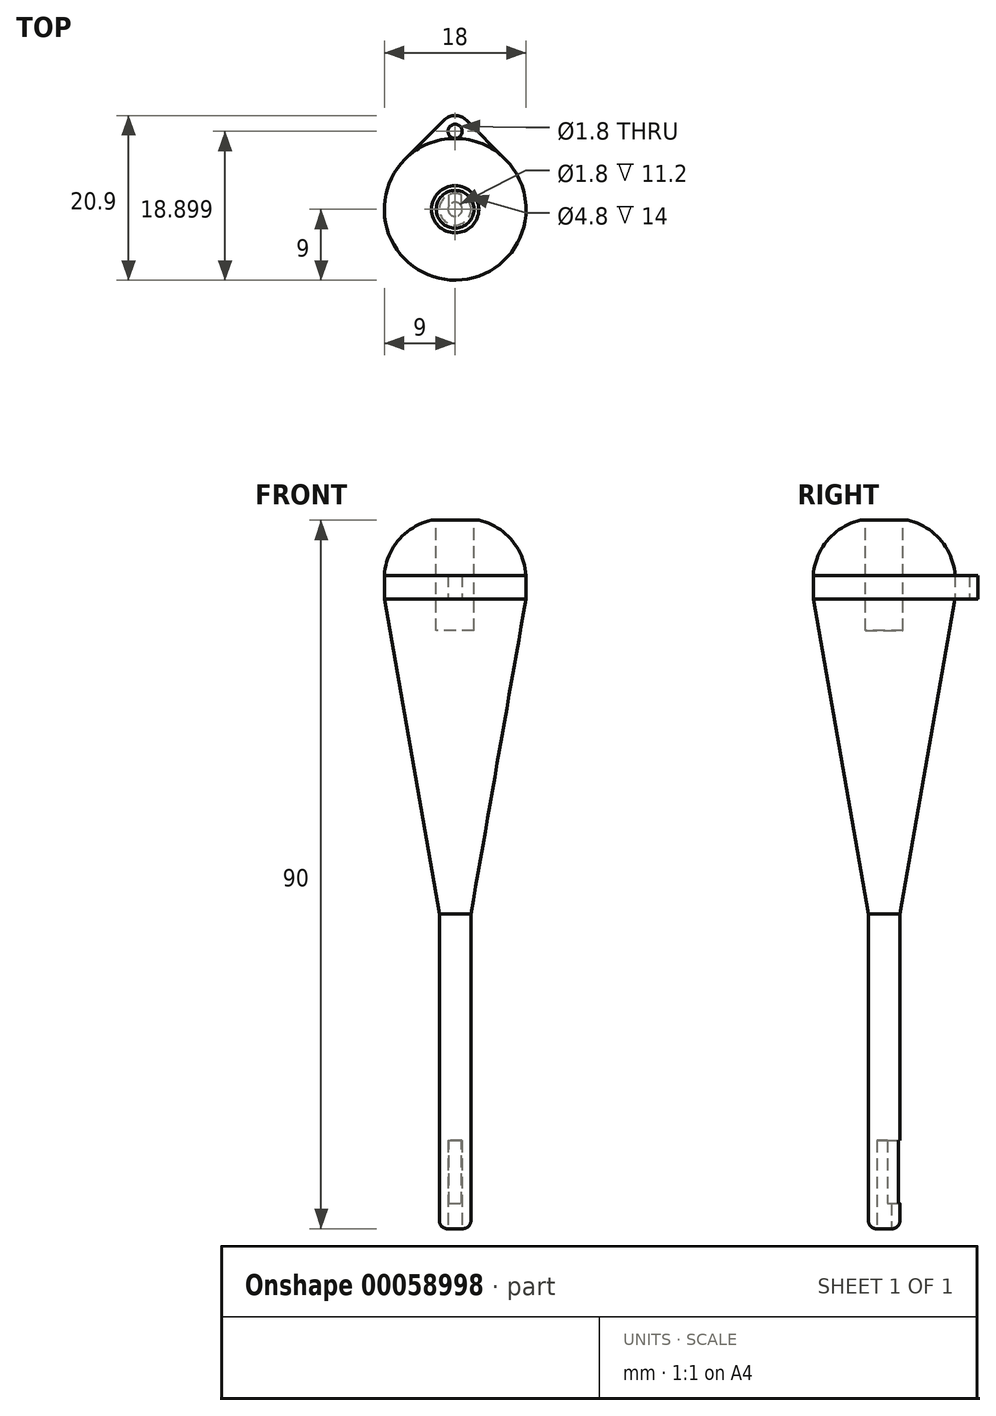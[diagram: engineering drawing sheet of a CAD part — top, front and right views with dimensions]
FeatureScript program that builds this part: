
annotation { "Feature Type Name" : "Feature", "Feature Type Description" : "" }
export const myFeature = defineFeature(function(context is Context, id is Id, definition is map)
    precondition{}
    {
        {
            var Q0;
            Q0=qCreatedBy(makeId("Top.planeOp"),FACE);
            var sketch = newSketch(context, id + "F0", { "sketchPlane" : qUnion([Q0])});
            skArc(sketch, "E0", {"start": v(-6.36, 6.36) * mm, "mid": v(0, -9) * mm, "end": v(6.36, 6.36) * mm});
            skLineSegment(sketch, "E1", {"start": v(-6.36, 6.36) * mm, "end": v(-1.41, 11.31) * mm});
            skLineSegment(sketch, "E2", {"start": v(1.41, 11.31) * mm, "end": v(6.36, 6.36) * mm});
            skPoint(sketch, "E3.visualSharp", {"position": v(0, 12.73) * mm});
            skArc(sketch, "E3.filletArc", {"start": v(1.41, 11.31) * mm, "mid": v(0, 11.9) * mm, "end": v(-1.41, 11.31) * mm});
            skLineSegment(sketch, "E4", {"start": v(0, 0) * mm, "end": v(10.96, 10.96) * mm, "construction": true});
            skCircle(sketch, "E5", {"center": v(0, 0) * mm, "radius": 9 * mm, "construction": true});
            skCircle(sketch, "E6", {"center": v(0, 9.9) * mm, "radius": 0.9 * mm});
            skSolve(sketch);
        }
        {
            var Q0;
            Q0 = qSketchRegion(id + "F0", true);
            extrude(context, id + "F1", {"entities" : qUnion([Q0]), "depth" : 3 * mm});
        }
        {
            var Q0;
            Q0=qCreatedBy(makeId("Right.planeOp"),FACE);
            var sketch = newSketch(context, id + "F2", { "sketchPlane" : qUnion([Q0])});
            skLineSegment(sketch, "E7", {"start": v(0, 3) * mm, "end": v(0, 10) * mm});
            skLineSegment(sketch, "E8", {"start": v(0, 10) * mm, "end": v(3, 10) * mm});
            skLineSegment(sketch, "E9", {"start": v(0, 3) * mm, "end": v(9, 3) * mm});
            skArc(sketch, "E10", {"start": v(9, 3) * mm, "mid": v(7.16, 7.5) * mm, "end": v(3, 10) * mm});
            skLineSegment(sketch, "E11", {"start": v(0, 0) * mm, "end": v(0, -80) * mm});
            skLineSegment(sketch, "E12", {"start": v(0, -80) * mm, "end": v(1, -80) * mm});
            skLineSegment(sketch, "E13", {"start": v(2, -79) * mm, "end": v(2, -40) * mm});
            skLineSegment(sketch, "E14", {"start": v(2, -40) * mm, "end": v(9, 0) * mm});
            skLineSegment(sketch, "E15", {"start": v(9, 0) * mm, "end": v(0, 0) * mm});
            skPoint(sketch, "E16.visualSharp", {"position": v(2, -80) * mm});
            skArc(sketch, "E16.filletArc", {"start": v(1, -80) * mm, "mid": v(1.7, -79.7) * mm, "end": v(2, -79) * mm});
            skSolve(sketch);
        }
        {
            var Q0;
            Q0 = qSketchRegion(id + "F2", true);
            var Q1;
            Q1=sQuery(id+"F2.wireOp",EDGE,"E11");
            revolve(context, id + "F3", {"operationType" : NewBodyOperationType.ADD, "entities" : qUnion([Q0]), "axis" : qUnion([Q1]), "revolveType" : RevolveType.FULL});
        }
        {
            var Q0;
            Q0=qCreatedBy(makeId("Front.planeOp"),FACE);
            cPlane(context, id + "F4", {"entities" : qUnion([Q0]), "cplaneType" : CPlaneType.OFFSET, "offset" : 9 * mm, "oppositeDirection" : true, "width" : 150 * mm, "height" : 150 * mm});
        }
        {
            var Q0;
            Q0=qCreatedBy(id+"F4.planeOp",FACE);
            var sketch = newSketch(context, id + "F5", { "sketchPlane" : qUnion([Q0])});
            skLineSegment(sketch, "E17", {"start": v(0, 0) * mm, "end": v(0, -61.52) * mm, "construction": true});
            skLineSegment(sketch, "E18.bottom", {"start": v(0.8, -76.8) * mm, "end": v(-0.8, -76.8) * mm});
            skLineSegment(sketch, "E18.top", {"start": v(0.8, -68.8) * mm, "end": v(-0.8, -68.8) * mm});
            skLineSegment(sketch, "E18.left", {"start": v(0.8, -76.8) * mm, "end": v(0.8, -68.8) * mm});
            skLineSegment(sketch, "E18.right", {"start": v(-0.8, -76.8) * mm, "end": v(-0.8, -68.8) * mm});
            skSolve(sketch);
        }
        {
            var Q0;
            Q0 = qSketchRegion(id + "F5", true);
            extrude(context, id + "F6", {"entities" : qUnion([Q0]), "operationType" : NewBodyOperationType.REMOVE, "depth" : 9 * mm});
        }
        {
            var Q0;
            Q0=makeQuery(id+"F3.opRevolve","SWEPT_FACE",FACE,{"disambiguationData":[OSD([sQuery(id+"F2.wireOp",EDGE,"E12")])]});
            var sketch = newSketch(context, id + "F7", { "sketchPlane" : qUnion([Q0])});
            skCircle(sketch, "E19", {"center": v(0, 0) * mm, "radius": 0.9 * mm});
            skSolve(sketch);
        }
        {
            var Q0;
            Q0 = qSketchRegion(id + "F7", true);
            extrude(context, id + "F8", {"entities" : qUnion([Q0]), "operationType" : NewBodyOperationType.REMOVE, "oppositeDirection" : true, "depth" : 11.2 * mm});
        }
        {
            var Q0;
            Q0=makeQuery(id+"F3.opRevolve","SWEPT_FACE",FACE,{"disambiguationData":[OSD([sQuery(id+"F2.wireOp",EDGE,"E8")])]});
            var sketch = newSketch(context, id + "F9", { "sketchPlane" : qUnion([Q0])});
            skCircle(sketch, "E20", {"center": v(0, 0) * mm, "radius": 2.4 * mm});
            skSolve(sketch);
        }
        {
            var Q0;
            Q0 = qSketchRegion(id + "F9", true);
            extrude(context, id + "F10", {"entities" : qUnion([Q0]), "operationType" : NewBodyOperationType.REMOVE, "oppositeDirection" : true, "depth" : 14 * mm});
        }
    });
